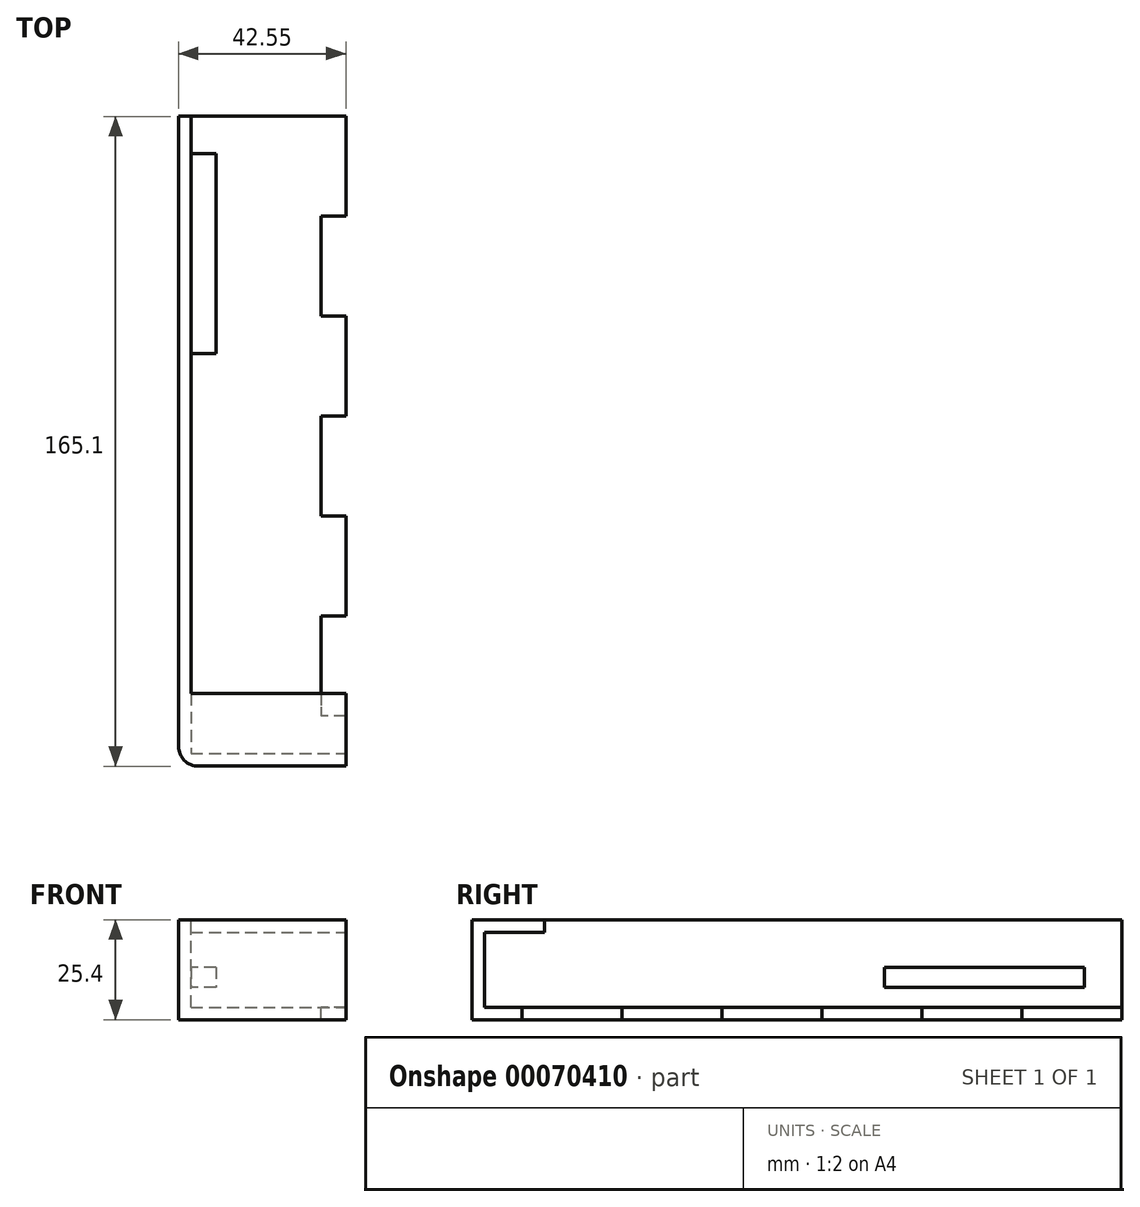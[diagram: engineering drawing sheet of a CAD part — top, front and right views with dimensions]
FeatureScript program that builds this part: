
annotation { "Feature Type Name" : "Feature", "Feature Type Description" : "" }
export const myFeature = defineFeature(function(context is Context, id is Id, definition is map)
    precondition{}
    {
        {
            var Q0;
            Q0=qCreatedBy(makeId("Top.planeOp"),FACE);
            var sketch = newSketch(context, id + "F0", { "sketchPlane" : qUnion([Q0])});
            skLineSegment(sketch, "E0.bottom", {"start": v(-64.58, 80.8) * mm, "end": v(-22.03, 80.8) * mm});
            skLineSegment(sketch, "E0.top", {"start": v(-64.58, -84.3) * mm, "end": v(-22.03, -84.3) * mm});
            skLineSegment(sketch, "E0.left", {"start": v(-64.58, 80.8) * mm, "end": v(-64.58, -84.3) * mm});
            skLineSegment(sketch, "E0.right", {"start": v(-22.03, 80.8) * mm, "end": v(-22.03, -84.3) * mm});
            skSolve(sketch);
        }
        {
            var Q0;
            Q0=makeQuery(id+"F0.imprint","IMPRINT",FACE,{"disambiguationData":[TD([[makeQuery(id+"F0.imprint","IMPRINT",EDGE,{"derivedFrom":sQuery(id+"F0.wireOp",EDGE,"E0.bottom")}),-1.0]])]});
            extrude(context, id + "F1", {"entities" : qUnion([Q0]), "depth" : 25.4 * mm});
        }
        {
            var Q0;
            Q0=makeQuery(id+"F1.opExtrude","CAP_FACE",FACE,{"disambiguationData":[OSD([sQuery(id+"F0.wireOp",EDGE,"E0.bottom"),sQuery(id+"F0.wireOp",EDGE,"E0.top"),sQuery(id+"F0.wireOp",EDGE,"E0.left"),sQuery(id+"F0.wireOp",EDGE,"E0.right")])],"isStart":false});
            var sketch = newSketch(context, id + "F2", { "sketchPlane" : qUnion([Q0])});
            skLineSegment(sketch, "E1.0", {"start": v(-61.4, -81.12) * mm, "end": v(-22.03, -81.12) * mm});
            skLineSegment(sketch, "E1.1", {"start": v(-61.4, 80.8) * mm, "end": v(-61.4, -81.12) * mm});
            skSolve(sketch);
        }
        {
            var Q0;
            {var subQ0=sQuery(id+"F2.wireOp",EDGE,"E1.0");Q0=makeQuery(id+"F2.imprint","IMPRINT",FACE,{"disambiguationData":[TD([[makeQuery(id+"F2.imprint","IMPRINT",EDGE,{"derivedFrom":subQ0}),1.0]])]});}
            extrude(context, id + "F3", {"entities" : qUnion([Q0]), "operationType" : NewBodyOperationType.REMOVE, "oppositeDirection" : true, "depth" : 22.22 * mm});
        }
        {
            var Q0;
            Q0=makeQuery(id+"F1.opExtrude","CAP_FACE",FACE,{"disambiguationData":[OSD([sQuery(id+"F0.wireOp",EDGE,"E0.bottom"),sQuery(id+"F0.wireOp",EDGE,"E0.top"),sQuery(id+"F0.wireOp",EDGE,"E0.left"),sQuery(id+"F0.wireOp",EDGE,"E0.right")])],"isStart":false});
            var sketch = newSketch(context, id + "F4", { "sketchPlane" : qUnion([Q0])});
            skLineSegment(sketch, "E2.bottom", {"start": v(-22.03, -81.12) * mm, "end": v(-61.4, -81.12) * mm});
            skLineSegment(sketch, "E2.top", {"start": v(-22.03, -65.88) * mm, "end": v(-61.4, -65.88) * mm});
            skLineSegment(sketch, "E2.left", {"start": v(-22.03, -81.12) * mm, "end": v(-22.03, -65.88) * mm});
            skLineSegment(sketch, "E2.right", {"start": v(-61.4, -81.12) * mm, "end": v(-61.4, -65.88) * mm});
            skSolve(sketch);
        }
        {
            var Q0;
            Q0=makeQuery(id+"F4.imprint","IMPRINT",FACE,{"disambiguationData":[TD([[makeQuery(id+"F4.imprint","IMPRINT",EDGE,{"derivedFrom":sQuery(id+"F4.wireOp",EDGE,"E2.bottom")}),1.0]])]});
            extrude(context, id + "F5", {"entities" : qUnion([Q0]), "operationType" : NewBodyOperationType.ADD, "oppositeDirection" : true, "depth" : 3.17 * mm});
        }
        {
            var Q0;
            Q0=makeQuery(id+"F3.boolean.opBoolean","COPY",FACE,{"derivedFrom":makeQuery(id+"F3.opExtrude","SWEPT_FACE",FACE,{"disambiguationData":[OSD([sQuery(id+"F2.wireOp",EDGE,"E1.1")])]})});
            var sketch = newSketch(context, id + "F6", { "sketchPlane" : qUnion([Q0])});
            skLineSegment(sketch, "E3.bottom", {"start": v(71.28, 13.34) * mm, "end": v(20.48, 13.33) * mm});
            skLineSegment(sketch, "E3.top", {"start": v(71.28, 8.26) * mm, "end": v(20.48, 8.25) * mm});
            skLineSegment(sketch, "E3.left", {"start": v(71.28, 13.34) * mm, "end": v(71.28, 8.26) * mm});
            skLineSegment(sketch, "E3.right", {"start": v(20.48, 13.33) * mm, "end": v(20.48, 8.25) * mm});
            skSolve(sketch);
        }
        {
            var Q0;
            Q0=makeQuery(id+"F6.imprint","IMPRINT",FACE,{"disambiguationData":[TD([[makeQuery(id+"F6.imprint","IMPRINT",EDGE,{"derivedFrom":sQuery(id+"F6.wireOp",EDGE,"E3.bottom")}),1.0]])]});
            extrude(context, id + "F7", {"entities" : qUnion([Q0]), "operationType" : NewBodyOperationType.ADD, "depth" : 6.35 * mm});
        }
        {
            var Q0;
            Q0=makeQuery(id+"F3.boolean.opBoolean","COPY",FACE,{"derivedFrom":makeQuery(id+"F3.opExtrude","CAP_FACE",FACE,{"disambiguationData":[OSD([sQuery(id+"F0.wireOp",EDGE,"E0.bottom"),sQuery(id+"F0.wireOp",EDGE,"E0.right"),sQuery(id+"F2.wireOp",EDGE,"E1.0"),sQuery(id+"F2.wireOp",EDGE,"E1.1")])],"isStart":false})});
            var sketch = newSketch(context, id + "F8", { "sketchPlane" : qUnion([Q0])});
            skLineSegment(sketch, "E4.bottom", {"start": v(-22.03, 55.4) * mm, "end": v(-28.38, 55.4) * mm});
            skLineSegment(sketch, "E4.top", {"start": v(-22.03, 30) * mm, "end": v(-28.38, 30) * mm});
            skLineSegment(sketch, "E4.left", {"start": v(-22.03, 55.4) * mm, "end": v(-22.03, 30) * mm});
            skLineSegment(sketch, "E4.right", {"start": v(-28.38, 55.4) * mm, "end": v(-28.38, 30) * mm});
            skLineSegment(sketch, "E5.0.1.0", {"start": v(-28.38, 4.6) * mm, "end": v(-28.38, -20.8) * mm});
            skLineSegment(sketch, "E5.0.1.1", {"start": v(-22.03, 4.6) * mm, "end": v(-28.38, 4.6) * mm});
            skLineSegment(sketch, "E5.0.1.2", {"start": v(-22.03, 4.6) * mm, "end": v(-22.03, -20.8) * mm});
            skLineSegment(sketch, "E5.0.1.3", {"start": v(-22.03, -20.8) * mm, "end": v(-28.38, -20.8) * mm});
            skLineSegment(sketch, "E5.0.2.0", {"start": v(-28.38, -46.2) * mm, "end": v(-28.38, -71.6) * mm});
            skLineSegment(sketch, "E5.0.2.1", {"start": v(-22.03, -46.2) * mm, "end": v(-28.38, -46.2) * mm});
            skLineSegment(sketch, "E5.0.2.2", {"start": v(-22.03, -46.2) * mm, "end": v(-22.03, -71.6) * mm});
            skLineSegment(sketch, "E5.0.2.3", {"start": v(-22.03, -71.6) * mm, "end": v(-28.38, -71.6) * mm});
            skLineSegment(sketch, "E5.direction1", {"start": v(-28.38, 30) * mm, "end": v(-2.98, 30) * mm, "construction": true});
            skLineSegment(sketch, "E5.direction2", {"start": v(-28.38, 30) * mm, "end": v(-28.38, -20.8) * mm, "construction": true});
            skSolve(sketch);
        }
        {
            var Q0;
            Q0=makeQuery(id+"F8.imprint","IMPRINT",FACE,{"disambiguationData":[TD([[makeQuery(id+"F8.imprint","IMPRINT",EDGE,{"derivedFrom":sQuery(id+"F8.wireOp",EDGE,"E5.0.2.0")}),1.0]])]});
            var Q1;
            Q1=makeQuery(id+"F8.imprint","IMPRINT",FACE,{"disambiguationData":[TD([[makeQuery(id+"F8.imprint","IMPRINT",EDGE,{"derivedFrom":sQuery(id+"F8.wireOp",EDGE,"E5.0.1.0")}),1.0]])]});
            var Q2;
            Q2=makeQuery(id+"F8.imprint","IMPRINT",FACE,{"disambiguationData":[TD([[makeQuery(id+"F8.imprint","IMPRINT",EDGE,{"derivedFrom":sQuery(id+"F8.wireOp",EDGE,"E4.bottom")}),1.0]])]});
            extrude(context, id + "F9", {"entities" : qUnion([Q0, Q1, Q2]), "operationType" : NewBodyOperationType.REMOVE, "endBound" : BoundingType.THROUGH_ALL, "oppositeDirection" : true, "depth" : 25.4 * mm});
        }
        {
            var Q0;
            Q0=makeQuery(id+"F1.opExtrude","SWEPT_EDGE",EDGE,{"disambiguationData":[OSD([sQuery(id+"F0.wireOp",EDGE,"E0.top"),sQuery(id+"F0.wireOp",EDGE,"E0.left")])]});
            fillet(context, id + "F10", {"entities" : qUnion([Q0]), "radius" : 5.08 * mm, "tangentPropagation" : true, "allowEdgeOverflow" : false});
        }
    });
